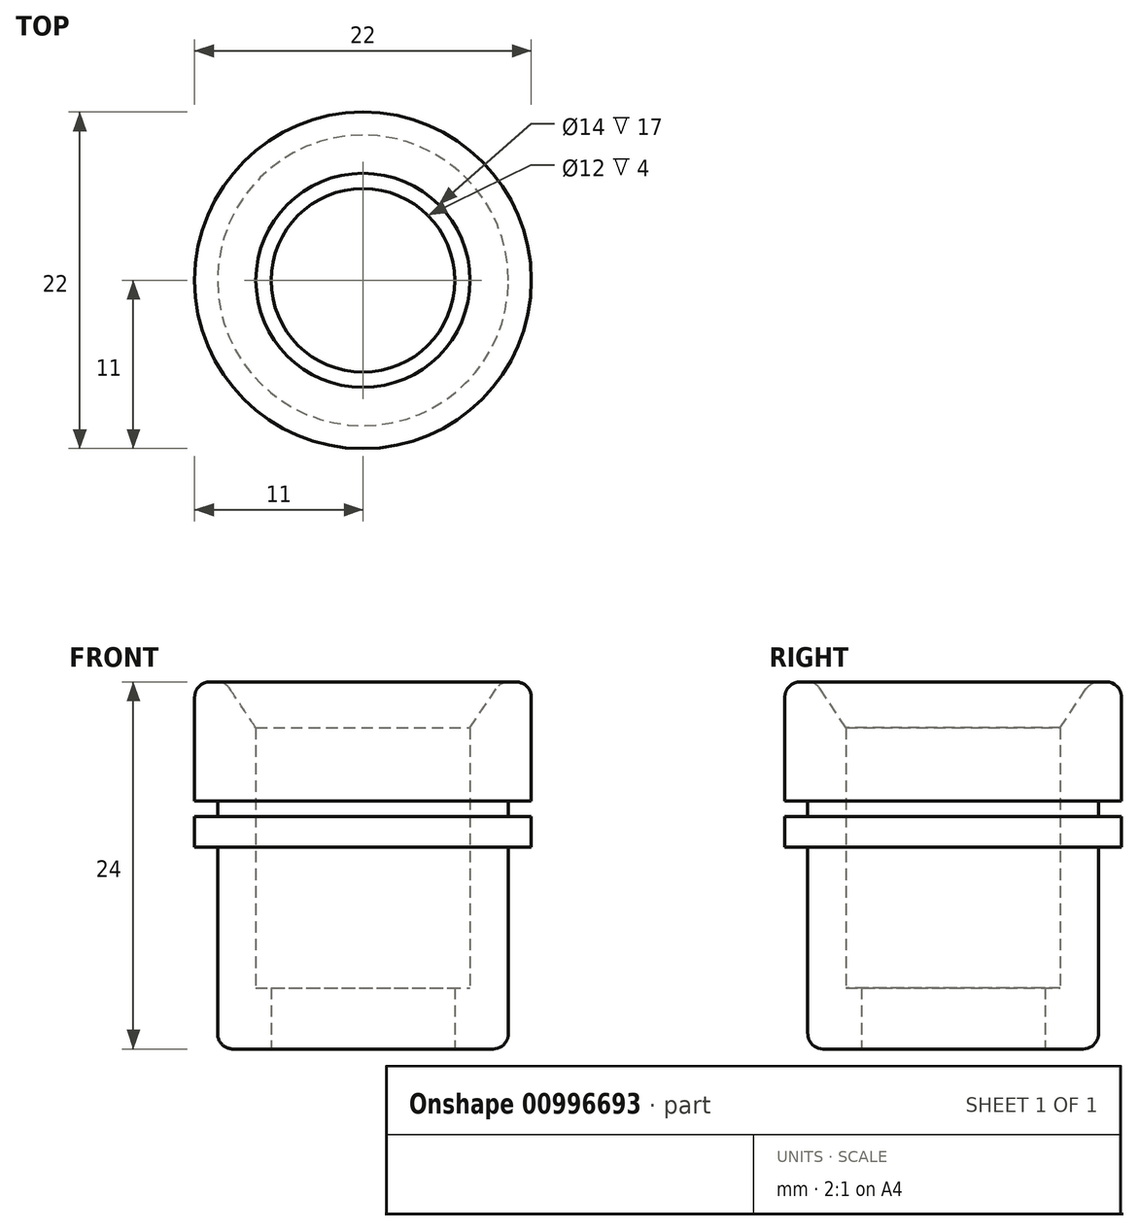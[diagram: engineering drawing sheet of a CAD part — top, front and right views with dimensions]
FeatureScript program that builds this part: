
annotation { "Feature Type Name" : "Feature", "Feature Type Description" : "" }
export const myFeature = defineFeature(function(context is Context, id is Id, definition is map)
    precondition{}
    {
        {
            var Q0;
            Q0=qCreatedBy(makeId("Front.planeOp"),FACE);
            var sketch = newSketch(context, id + "F0", { "sketchPlane" : qUnion([Q0])});
            skLineSegment(sketch, "E0", {"start": v(7, 4) * mm, "end": v(6, 4) * mm});
            skLineSegment(sketch, "E1", {"start": v(6, 4) * mm, "end": v(6, 0) * mm});
            skLineSegment(sketch, "E2", {"start": v(6, 0) * mm, "end": v(9.5, 0) * mm});
            skLineSegment(sketch, "E3", {"start": v(9.5, 0) * mm, "end": v(9.5, 13.2) * mm});
            skLineSegment(sketch, "E4", {"start": v(9.5, 13.2) * mm, "end": v(11, 13.2) * mm});
            skLineSegment(sketch, "E5", {"start": v(11, 13.2) * mm, "end": v(11, 15.2) * mm});
            skLineSegment(sketch, "E6", {"start": v(11, 15.2) * mm, "end": v(9.5, 15.2) * mm});
            skLineSegment(sketch, "E7", {"start": v(9.5, 15.2) * mm, "end": v(9.5, 16.2) * mm});
            skLineSegment(sketch, "E8", {"start": v(9.5, 16.2) * mm, "end": v(11, 16.2) * mm});
            skLineSegment(sketch, "E9", {"start": v(11, 16.2) * mm, "end": v(11, 24) * mm});
            skLineSegment(sketch, "E10", {"start": v(11, 24) * mm, "end": v(9, 24) * mm});
            skLineSegment(sketch, "E11", {"start": v(7, 21) * mm, "end": v(7, 4) * mm});
            skLineSegment(sketch, "E12", {"start": v(0, -6.73) * mm, "end": v(0, 49.78) * mm, "construction": true});
            skLineSegment(sketch, "E13", {"start": v(9, 24) * mm, "end": v(7, 21) * mm});
            skPoint(sketch, "E14.orphan", {"position": v(7, 24) * mm});
            skSolve(sketch);
        }
        {
            var Q0;
            Q0=makeQuery(id+"F0.imprint","IMPRINT",FACE,{"disambiguationData":[TD([[makeQuery(id+"F0.imprint","IMPRINT",EDGE,{"derivedFrom":sQuery(id+"F0.wireOp",EDGE,"E0")}),1.0]])]});
            var Q1;
            Q1=sQuery(id+"F0.wireOp",EDGE,"E12");
            revolve(context, id + "F1", {"surfaceOperationType" : NewSurfaceOperationType.NEW, "entities" : qUnion([Q0]), "axis" : qUnion([Q1]), "revolveType" : RevolveType.FULL});
        }
        {
            var Q0;
            Q0=makeQuery(id+"F1.opRevolve","SWEPT_EDGE",EDGE,{"disambiguationData":[OSD([sQuery(id+"F0.wireOp",EDGE,"E9"),sQuery(id+"F0.wireOp",EDGE,"E10")])]});
            var Q1;
            Q1=makeQuery(id+"F1.opRevolve","SWEPT_EDGE",EDGE,{"disambiguationData":[OSD([sQuery(id+"F0.wireOp",EDGE,"E10"),sQuery(id+"F0.wireOp",EDGE,"E13")])]});
            var Q2;
            Q2=makeQuery(id+"F1.opRevolve","SWEPT_EDGE",EDGE,{"disambiguationData":[OSD([sQuery(id+"F0.wireOp",EDGE,"E2"),sQuery(id+"F0.wireOp",EDGE,"E3")])]});
            fillet(context, id + "F2", {"entities" : qUnion([Q0, Q1, Q2]), "radius" : 1 * mm, "tangentPropagation" : true, "allowEdgeOverflow" : false});
        }
    });
